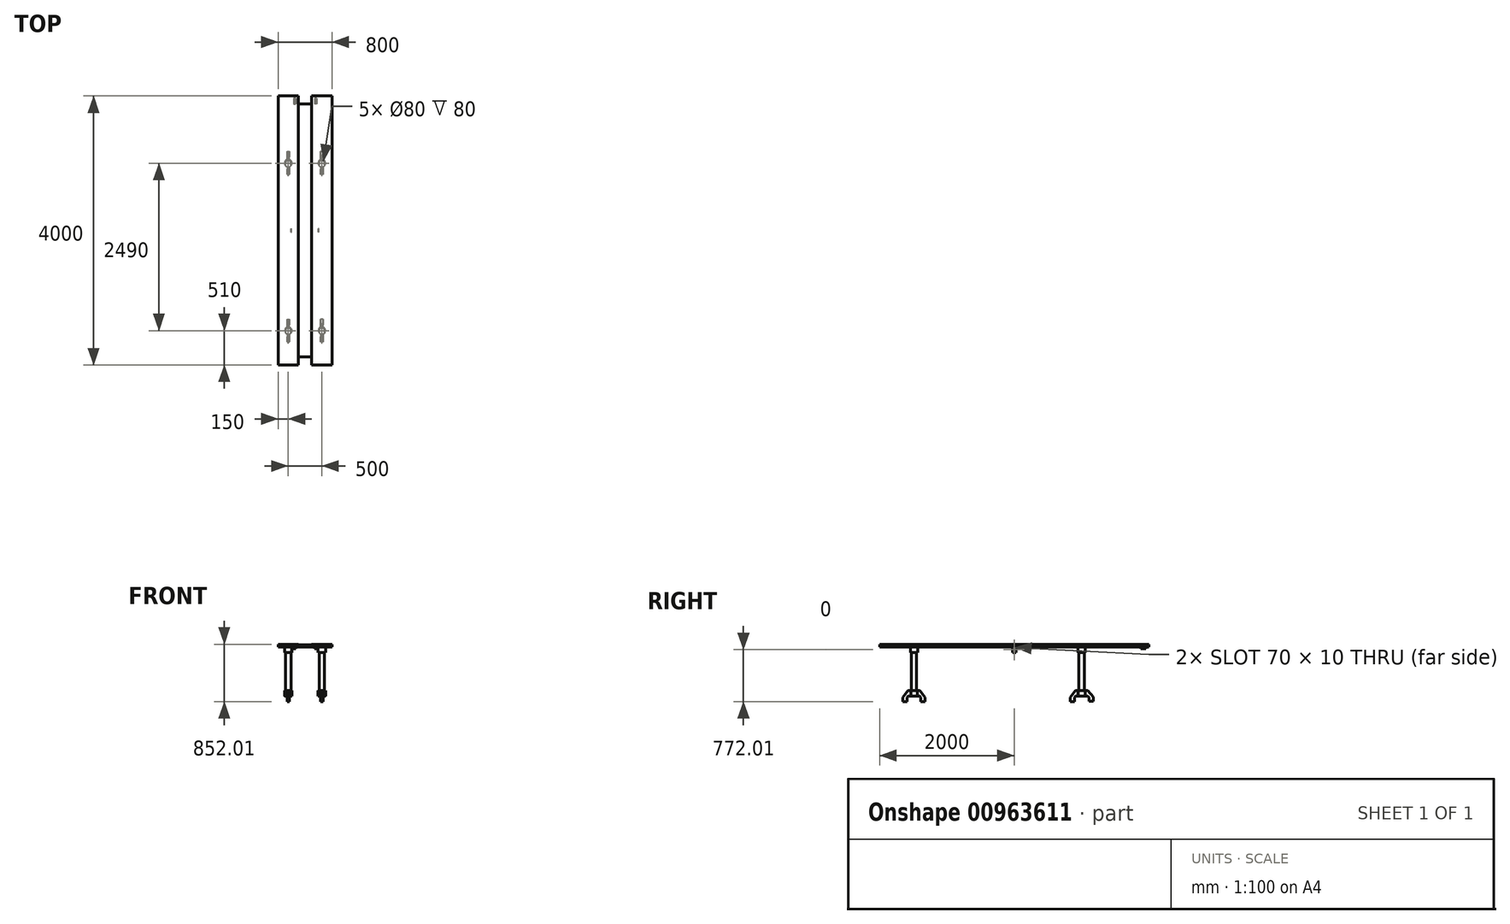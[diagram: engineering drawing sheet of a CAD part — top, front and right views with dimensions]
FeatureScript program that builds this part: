
annotation { "Feature Type Name" : "Feature", "Feature Type Description" : "" }
export const myFeature = defineFeature(function(context is Context, id is Id, definition is map)
    precondition{}
    {
        {
            var Q0;
            Q0=qCreatedBy(makeId("Front.planeOp"),FACE);
            var sketch = newSketch(context, id + "F0", { "sketchPlane" : qUnion([Q0])});
            skLineSegment(sketch, "E0", {"start": v(0, 63.58) * mm, "end": v(0, -44.48) * mm, "construction": true});
            skLineSegment(sketch, "E1", {"start": v(-61.04, 0) * mm, "end": v(60.75, 0) * mm, "construction": true});
            skLineSegment(sketch, "E2", {"start": v(-100, 20) * mm, "end": v(-400, 20) * mm});
            skLineSegment(sketch, "E3", {"start": v(-400, 20) * mm, "end": v(-400, -20) * mm});
            skLineSegment(sketch, "E4", {"start": v(-400, -20) * mm, "end": v(400, -20) * mm});
            skLineSegment(sketch, "E5", {"start": v(400, -20) * mm, "end": v(400, 20) * mm});
            skLineSegment(sketch, "E6", {"start": v(400, 20) * mm, "end": v(100, 20) * mm});
            skLineSegment(sketch, "E7", {"start": v(100, 20) * mm, "end": v(100, 10) * mm});
            skLineSegment(sketch, "E8", {"start": v(100, 10) * mm, "end": v(-100, 10) * mm});
            skLineSegment(sketch, "E9", {"start": v(-100, 10) * mm, "end": v(-100, 20) * mm});
            skSolve(sketch);
        }
        {
            var Q0;
            Q0 = qSketchRegion(id + "F0", true);
            extrude(context, id + "F1", {"entities" : qUnion([Q0]), "oppositeDirection" : true, "depth" : 4000 * mm, "offsetDistance" : 25.4 * mm});
        }
        {
            var Q0;
            Q0=makeQuery(id+"F1.opExtrude","SWEPT_FACE",FACE,{"disambiguationData":[OSD([sQuery(id+"F0.wireOp",EDGE,"E8")])]});
            var sketch = newSketch(context, id + "F2", { "sketchPlane" : qUnion([Q0])});
            skLineSegment(sketch, "E10.bottom", {"start": v(-100, 0) * mm, "end": v(100, 0) * mm});
            skLineSegment(sketch, "E10.top", {"start": v(-100, 120) * mm, "end": v(100, 120) * mm});
            skLineSegment(sketch, "E10.left", {"start": v(-100, 0) * mm, "end": v(-100, 120) * mm});
            skLineSegment(sketch, "E10.right", {"start": v(100, 0) * mm, "end": v(100, 120) * mm});
            skLineSegment(sketch, "E11.bottom", {"start": v(-100, 4000) * mm, "end": v(100, 4000) * mm});
            skLineSegment(sketch, "E11.top", {"start": v(-100, 3880) * mm, "end": v(100, 3880) * mm});
            skLineSegment(sketch, "E11.left", {"start": v(-100, 4000) * mm, "end": v(-100, 3880) * mm});
            skLineSegment(sketch, "E11.right", {"start": v(100, 4000) * mm, "end": v(100, 3880) * mm});
            skSolve(sketch);
        }
        {
            var Q0;
            Q0 = qSketchRegion(id + "F2", true);
            extrude(context, id + "F3", {"entities" : qUnion([Q0]), "operationType" : NewBodyOperationType.REMOVE, "oppositeDirection" : true, "depth" : 55.88 * mm, "offsetDistance" : 25.4 * mm});
        }
        {
            var Q0;
            Q0=makeQuery(id+"F3.boolean.opBoolean","COPY",EDGE,{"derivedFrom":makeQuery(id+"F3.opExtrude","CAP_EDGE",EDGE,{"disambiguationData":[OSD([sQuery(id+"F2.wireOp",EDGE,"E11.top")])],"isStart":true})});
            var Q1;
            Q1=makeQuery(id+"F3.boolean.opBoolean","COPY",EDGE,{"derivedFrom":makeQuery(id+"F3.opExtrude","CAP_EDGE",EDGE,{"disambiguationData":[OSD([sQuery(id+"F2.wireOp",EDGE,"E10.top")])],"isStart":true})});
            var Q2;
            Q2=makeQuery(id+"F3.boolean.opBoolean","INTERSECT",EDGE,{"derivedFrom":[makeQuery(id+"F1.opExtrude","SWEPT_FACE",FACE,{"disambiguationData":[OSD([sQuery(id+"F0.wireOp",EDGE,"E4")])]}),makeQuery(id+"F3.opExtrude","SWEPT_FACE",FACE,{"disambiguationData":[OSD([sQuery(id+"F2.wireOp",EDGE,"E10.top")])]})]});
            var Q3;
            Q3=makeQuery(id+"F3.boolean.opBoolean","INTERSECT",EDGE,{"derivedFrom":[makeQuery(id+"F1.opExtrude","SWEPT_FACE",FACE,{"disambiguationData":[OSD([sQuery(id+"F0.wireOp",EDGE,"E4")])]}),makeQuery(id+"F3.opExtrude","SWEPT_FACE",FACE,{"disambiguationData":[OSD([sQuery(id+"F2.wireOp",EDGE,"E11.top")])]})]});
            fillet(context, id + "F4", {"entities" : qUnion([Q0, Q1, Q2, Q3]), "radius" : 10 * mm, "tangentPropagation" : true, "allowEdgeOverflow" : false});
        }
        {
            var Q0;
            Q0=makeQuery(id+"F1.opExtrude","SWEPT_FACE",FACE,{"disambiguationData":[OSD([sQuery(id+"F0.wireOp",EDGE,"E4")])]});
            var sketch = newSketch(context, id + "F5", { "sketchPlane" : qUnion([Q0])});
            skCircle(sketch, "E12", {"center": v(-250, -510) * mm, "radius": 55 * mm});
            skPoint(sketch, "E12.centerSnap0", {"position": v(-250, 0) * mm});
            skCircle(sketch, "E13", {"center": v(-250, -3000) * mm, "radius": 55 * mm});
            skPoint(sketch, "E13.centerSnap0", {"position": v(-250, -4000) * mm});
            skLineSegment(sketch, "E14", {"start": v(0, 313.38) * mm, "end": v(0, -4618.74) * mm, "construction": true});
            skCircle(sketch, "E15.MirrorC", {"center": v(250, -510) * mm, "radius": 55 * mm});
            skCircle(sketch, "E16.MirrorC", {"center": v(250, -3000) * mm, "radius": 55 * mm});
            skCircle(sketch, "E17", {"center": v(-250, -3000) * mm, "radius": 40 * mm});
            skCircle(sketch, "E18", {"center": v(-250, -510) * mm, "radius": 40 * mm});
            skCircle(sketch, "E19", {"center": v(250, -510) * mm, "radius": 40 * mm});
            skCircle(sketch, "E20", {"center": v(250, -3000) * mm, "radius": 40 * mm});
            skSolve(sketch);
        }
        {
            var Q0;
            Q0 = qSketchRegion(id + "F5", true);
            extrude(context, id + "F6", {"entities" : qUnion([Q0]), "operationType" : NewBodyOperationType.ADD, "depth" : 80 * mm, "offsetDistance" : 25.4 * mm});
        }
        {
            var Q0;
            {var subQ0=sQuery(id+"F0.wireOp",EDGE,"E3");var subQ1=sQuery(id+"F0.wireOp",EDGE,"E4");Q0=makeQuery(id+"F6.boolean.opBoolean","SPLIT",FACE,{"disambiguationData":[TD([makeQuery(id+"F1.opExtrude","SWEPT_FACE",FACE,{"disambiguationData":[OSD([subQ0])]})])],"derivedFrom":makeQuery(id+"F1.opExtrude","SWEPT_FACE",FACE,{"disambiguationData":[OSD([subQ1])]})});}
            var sketch = newSketch(context, id + "F7", { "sketchPlane" : qUnion([Q0])});
            skLineSegment(sketch, "E21.bottom", {"start": v(-205, -1975) * mm, "end": v(-200, -1975) * mm});
            skLineSegment(sketch, "E21.top", {"start": v(-205, -2025) * mm, "end": v(-200, -2025) * mm});
            skLineSegment(sketch, "E21.left", {"start": v(-205, -1975) * mm, "end": v(-205, -2025) * mm});
            skLineSegment(sketch, "E21.right", {"start": v(-200, -1975) * mm, "end": v(-200, -2025) * mm});
            skLineSegment(sketch, "E22.bottom", {"start": v(205, -1975) * mm, "end": v(200, -1975) * mm});
            skLineSegment(sketch, "E22.top", {"start": v(205, -2025) * mm, "end": v(200, -2025) * mm});
            skLineSegment(sketch, "E22.left", {"start": v(205, -1975) * mm, "end": v(205, -2025) * mm});
            skLineSegment(sketch, "E22.right", {"start": v(200, -1975) * mm, "end": v(200, -2025) * mm});
            skLineSegment(sketch, "E23", {"start": v(-691.2, -2000) * mm, "end": v(786.12, -2000) * mm, "construction": true});
            skPoint(sketch, "E23.startSnap0", {"position": v(-400, -2000) * mm});
            skLineSegment(sketch, "E24", {"start": v(0, 1136.46) * mm, "end": v(0, -4393.14) * mm, "construction": true});
            skSolve(sketch);
        }
        {
            var Q0;
            Q0 = qSketchRegion(id + "F7", true);
            extrude(context, id + "F8", {"entities" : qUnion([Q0]), "operationType" : NewBodyOperationType.ADD, "depth" : 80 * mm, "offsetDistance" : 25.4 * mm});
        }
        {
            var Q0;
            Q0=makeQuery(id+"F8.opExtrude","SWEPT_FACE",FACE,{"disambiguationData":[OSD([sQuery(id+"F7.wireOp",EDGE,"E21.left")])]});
            var sketch = newSketch(context, id + "F9", { "sketchPlane" : qUnion([Q0])});
            skLineSegment(sketch, "E25", {"start": v(-2000, -30) * mm, "end": v(-2000, -90) * mm, "construction": true});
            skPoint(sketch, "E25.startSnap0", {"position": v(-2000, -100) * mm});
            skArc(sketch, "E26", {"start": v(-1995, -30) * mm, "mid": v(-2000, -25) * mm, "end": v(-2005, -30) * mm});
            skLineSegment(sketch, "E27", {"start": v(-2005, -30) * mm, "end": v(-2005, -90) * mm});
            skLineSegment(sketch, "E28", {"start": v(-1995, -30) * mm, "end": v(-1995, -90) * mm});
            skArc(sketch, "E29", {"start": v(-2005, -90) * mm, "mid": v(-2000, -95) * mm, "end": v(-1995, -90) * mm});
            skSolve(sketch);
        }
        {
            var Q0;
            Q0 = qSketchRegion(id + "F9", true);
            extrude(context, id + "F10", {"entities" : qUnion([Q0]), "operationType" : NewBodyOperationType.REMOVE, "endBound" : BoundingType.THROUGH_ALL, "oppositeDirection" : true, "depth" : 25.4 * mm, "offsetDistance" : 25.4 * mm});
        }
        {
            var Q0;
            Q0=makeQuery(id+"F6.boolean.opBoolean","SPLIT",FACE,{"disambiguationData":[TD([makeQuery(id+"F6.opExtrude","SWEPT_FACE",FACE,{"disambiguationData":[OSD([sQuery(id+"F5.wireOp",EDGE,"E20")])]})])],"derivedFrom":makeQuery(id+"F1.opExtrude","SWEPT_FACE",FACE,{"disambiguationData":[OSD([sQuery(id+"F0.wireOp",EDGE,"E4")])]})});
            var sketch = newSketch(context, id + "F11", { "sketchPlane" : qUnion([Q0])});
            skCircle(sketch, "E30", {"center": v(250, -3000) * mm, "radius": 40 * mm});
            skCircle(sketch, "E31", {"center": v(-250, -3000) * mm, "radius": 40 * mm});
            skCircle(sketch, "E32", {"center": v(-250, -510) * mm, "radius": 40 * mm});
            skCircle(sketch, "E33", {"center": v(250, -510) * mm, "radius": 40 * mm});
            skSolve(sketch);
        }
        {
            var Q0;
            Q0 = qSketchRegion(id + "F11", true);
            extrude(context, id + "F12", {"entities" : qUnion([Q0]), "operationType" : NewBodyOperationType.ADD, "depth" : 730 * mm, "offsetDistance" : 25.4 * mm});
        }
        {
            var Q0;
            Q0=makeQuery(id+"F12.opExtrude","CAP_FACE",FACE,{"disambiguationData":[OSD([sQuery(id+"F11.wireOp",EDGE,"E32")])],"isStart":false});
            var sketch = newSketch(context, id + "F13", { "sketchPlane" : qUnion([Q0])});
            skCircle(sketch, "E34", {"center": v(-250, -510) * mm, "radius": 40 * mm});
            skCircle(sketch, "E35", {"center": v(-250, -510) * mm, "radius": 50 * mm});
            skSolve(sketch);
        }
        {
            var Q0;
            Q0 = qSketchRegion(id + "F13", true);
            extrude(context, id + "F14", {"entities" : qUnion([Q0]), "oppositeDirection" : true, "depth" : 80 * mm, "offsetDistance" : 25.4 * mm});
        }
        {
            var Q0;
            Q0=makeQuery(id+"F14.opExtrude","CAP_EDGE",EDGE,{"disambiguationData":[OSD([sQuery(id+"F13.wireOp",EDGE,"E35")])],"isStart":true});
            cPlane(context, id + "F15", {"entities" : qUnion([Q0]), "cplaneType" : CPlaneType.LINE_ANGLE, "offset" : 25.4 * mm, "angle" : 0 * degree, "width" : 152.4 * mm, "height" : 152.4 * mm});
        }
        {
            var Q0;
            Q0=qCreatedBy(id+"F15.planeOp",FACE);
            var sketch = newSketch(context, id + "F16", { "sketchPlane" : qUnion([Q0])});
            skLineSegment(sketch, "E36", {"start": v(-558.17, -670) * mm, "end": v(-598.17, -670) * mm});
            skLineSegment(sketch, "E37", {"start": v(-598.17, -670) * mm, "end": v(-677, -767.01) * mm});
            skLineSegment(sketch, "E38", {"start": v(-677, -767.01) * mm, "end": v(-677, -832.01) * mm});
            skLineSegment(sketch, "E39", {"start": v(-677, -832.01) * mm, "end": v(-612, -832.01) * mm});
            skLineSegment(sketch, "E40", {"start": v(-612, -832.01) * mm, "end": v(-612, -767.01) * mm});
            skLineSegment(sketch, "E41", {"start": v(-612, -767.01) * mm, "end": v(-598.17, -750) * mm});
            skLineSegment(sketch, "E42", {"start": v(-598.17, -750) * mm, "end": v(-558.17, -750) * mm});
            skLineSegment(sketch, "E43", {"start": v(-558.17, -750) * mm, "end": v(-558.17, -670) * mm});
            skLineSegment(sketch, "E44", {"start": v(-462.75, -670) * mm, "end": v(-422.75, -670) * mm});
            skLineSegment(sketch, "E45", {"start": v(-422.75, -670) * mm, "end": v(-343.93, -767.01) * mm});
            skLineSegment(sketch, "E46", {"start": v(-343.93, -767.01) * mm, "end": v(-343.93, -832.01) * mm});
            skLineSegment(sketch, "E47", {"start": v(-343.93, -832.01) * mm, "end": v(-408.93, -832.01) * mm});
            skLineSegment(sketch, "E48", {"start": v(-408.93, -832.01) * mm, "end": v(-408.93, -767.01) * mm});
            skLineSegment(sketch, "E49", {"start": v(-408.93, -767.01) * mm, "end": v(-422.75, -750) * mm});
            skLineSegment(sketch, "E50", {"start": v(-422.75, -750) * mm, "end": v(-462.75, -750) * mm});
            skLineSegment(sketch, "E51", {"start": v(-462.75, -750) * mm, "end": v(-462.75, -670) * mm});
            skSolve(sketch);
        }
        {
            var Q0;
            Q0 = qSketchRegion(id + "F16", true);
            extrude(context, id + "F17", {"entities" : qUnion([Q0]), "operationType" : NewBodyOperationType.ADD, "endBound" : BoundingType.SYMMETRIC, "depth" : 33 * mm, "offsetDistance" : 25.4 * mm});
        }
        {
            var Q0;
            Q0=makeQuery(id+"F14.opExtrude","SWEPT_BODY",BODY,{"disambiguationData":[OSD([sQuery(id+"F13.wireOp",EDGE,"E34"),sQuery(id+"F13.wireOp",EDGE,"E35")])]});
            var Q1;
            Q1=qCreatedBy(makeId("Right.planeOp"),FACE);
            mirror(context, id + "F18", {"entities" : qUnion([Q0]), "mirrorPlane" : qUnion([Q1])});
        }
        {
            var Q0;
            Q0=makeQuery(id+"F12.opExtrude","CAP_FACE",FACE,{"disambiguationData":[OSD([sQuery(id+"F11.wireOp",EDGE,"E30")])],"isStart":false});
            var sketch = newSketch(context, id + "F19", { "sketchPlane" : qUnion([Q0])});
            skCircle(sketch, "E52", {"center": v(-250, -3000) * mm, "radius": 40 * mm});
            skCircle(sketch, "E53", {"center": v(-250, -3000) * mm, "radius": 55 * mm});
            skSolve(sketch);
        }
        {
            var Q0;
            Q0 = qSketchRegion(id + "F19", true);
            extrude(context, id + "F20", {"entities" : qUnion([Q0]), "oppositeDirection" : true, "depth" : 80 * mm, "offsetDistance" : 25.4 * mm});
        }
        {
            var Q0;
            Q0=makeQuery(id+"F20.opExtrude","SWEPT_BODY",BODY,{"disambiguationData":[OSD([sQuery(id+"F19.wireOp",EDGE,"E52"),sQuery(id+"F19.wireOp",EDGE,"E53")])]});
            var Q1;
            Q1=qCreatedBy(makeId("Right.planeOp"),FACE);
            mirror(context, id + "F21", {"entities" : qUnion([Q0]), "mirrorPlane" : qUnion([Q1])});
        }
        {
            var Q0;
            Q0=makeQuery(id+"F20.opExtrude","CAP_EDGE",EDGE,{"disambiguationData":[OSD([sQuery(id+"F19.wireOp",EDGE,"E53")])],"isStart":true});
            cPlane(context, id + "F22", {"entities" : qUnion([Q0]), "cplaneType" : CPlaneType.LINE_ANGLE, "offset" : 25.4 * mm, "angle" : 0 * degree, "width" : 152.4 * mm, "height" : 152.4 * mm});
        }
        {
            var Q0;
            Q0=qCreatedBy(id+"F22.planeOp",FACE);
            var sketch = newSketch(context, id + "F23", { "sketchPlane" : qUnion([Q0])});
            skLineSegment(sketch, "E54", {"start": v(-2949.5, -670) * mm, "end": v(-2909.5, -670) * mm});
            skLineSegment(sketch, "E55", {"start": v(-2909.5, -670) * mm, "end": v(-2830.68, -767.01) * mm});
            skLineSegment(sketch, "E56", {"start": v(-2830.68, -767.01) * mm, "end": v(-2830.68, -832.01) * mm});
            skLineSegment(sketch, "E57", {"start": v(-2830.68, -832.01) * mm, "end": v(-2895.68, -832.01) * mm});
            skLineSegment(sketch, "E58", {"start": v(-2895.68, -832.01) * mm, "end": v(-2895.68, -767.01) * mm});
            skLineSegment(sketch, "E59", {"start": v(-2895.68, -767.01) * mm, "end": v(-2909.5, -750) * mm});
            skLineSegment(sketch, "E60", {"start": v(-2909.5, -750) * mm, "end": v(-2949.5, -750) * mm});
            skLineSegment(sketch, "E61", {"start": v(-2949.5, -750) * mm, "end": v(-2949.5, -670) * mm});
            skLineSegment(sketch, "E62", {"start": v(-3050.57, -670) * mm, "end": v(-3090.57, -670) * mm});
            skLineSegment(sketch, "E63", {"start": v(-3090.57, -670) * mm, "end": v(-3176.12, -761.14) * mm});
            skLineSegment(sketch, "E64", {"start": v(-3176.12, -761.14) * mm, "end": v(-3176.12, -826.14) * mm});
            skLineSegment(sketch, "E65", {"start": v(-3176.12, -826.14) * mm, "end": v(-3111.12, -826.14) * mm});
            skLineSegment(sketch, "E66", {"start": v(-3111.12, -826.14) * mm, "end": v(-3111.12, -771.89) * mm});
            skLineSegment(sketch, "E67", {"start": v(-3111.12, -771.89) * mm, "end": v(-3090.57, -750) * mm});
            skLineSegment(sketch, "E68", {"start": v(-3090.57, -750) * mm, "end": v(-3050.57, -750) * mm});
            skLineSegment(sketch, "E69", {"start": v(-3050.57, -750) * mm, "end": v(-3050.57, -670) * mm});
            skSolve(sketch);
        }
        {
            var Q0;
            Q0 = qSketchRegion(id + "F23", true);
            extrude(context, id + "F24", {"entities" : qUnion([Q0]), "operationType" : NewBodyOperationType.ADD, "endBound" : BoundingType.SYMMETRIC, "depth" : 33 * mm, "offsetDistance" : 25.4 * mm});
        }
        {
            var Q0;
            Q0=makeQuery(id+"F20.opExtrude","SWEPT_BODY",BODY,{"disambiguationData":[OSD([sQuery(id+"F19.wireOp",EDGE,"E52"),sQuery(id+"F19.wireOp",EDGE,"E53")])]});
            var Q1;
            Q1=qCreatedBy(makeId("Right.planeOp"),FACE);
            mirror(context, id + "F25", {"entities" : qUnion([Q0]), "mirrorPlane" : qUnion([Q1])});
        }
        {
            var Q0;
            {var subQ0=sQuery(id+"F0.wireOp",EDGE,"E3");var subQ1=sQuery(id+"F0.wireOp",EDGE,"E4");Q0=makeQuery(id+"F6.boolean.opBoolean","SPLIT",FACE,{"disambiguationData":[TD([makeQuery(id+"F1.opExtrude","SWEPT_FACE",FACE,{"disambiguationData":[OSD([subQ0])]})])],"derivedFrom":makeQuery(id+"F1.opExtrude","SWEPT_FACE",FACE,{"disambiguationData":[OSD([subQ1])]})});}
            var sketch = newSketch(context, id + "F26", { "sketchPlane" : qUnion([Q0])});
            skLineSegment(sketch, "E70.bottom", {"start": v(145, -3960) * mm, "end": v(140, -3960) * mm});
            skLineSegment(sketch, "E70.top", {"start": v(145, -3880) * mm, "end": v(140, -3880) * mm});
            skLineSegment(sketch, "E70.left", {"start": v(145, -3960) * mm, "end": v(145, -3880) * mm});
            skLineSegment(sketch, "E70.right", {"start": v(140, -3960) * mm, "end": v(140, -3880) * mm});
            skLineSegment(sketch, "E71.bottom", {"start": v(-140, -3960) * mm, "end": v(-145, -3960) * mm});
            skLineSegment(sketch, "E71.top", {"start": v(-140, -3880) * mm, "end": v(-145, -3880) * mm});
            skLineSegment(sketch, "E71.left", {"start": v(-140, -3960) * mm, "end": v(-140, -3880) * mm});
            skLineSegment(sketch, "E71.right", {"start": v(-145, -3960) * mm, "end": v(-145, -3880) * mm});
            skSolve(sketch);
        }
        {
            var Q0;
            Q0 = qSketchRegion(id + "F26", true);
            extrude(context, id + "F27", {"entities" : qUnion([Q0]), "operationType" : NewBodyOperationType.ADD, "depth" : 25.4 * mm, "offsetDistance" : 25.4 * mm});
        }
        {
            var Q0;
            Q0=makeQuery(id+"F27.opExtrude","SWEPT_FACE",FACE,{"disambiguationData":[OSD([sQuery(id+"F26.wireOp",EDGE,"E71.right")])]});
            var sketch = newSketch(context, id + "F28", { "sketchPlane" : qUnion([Q0])});
            skLineSegment(sketch, "E72.bottom", {"start": v(-3960, -45.4) * mm, "end": v(-3880, -45.4) * mm});
            skLineSegment(sketch, "E72.top", {"start": v(-3960, -40.4) * mm, "end": v(-3880, -40.4) * mm});
            skLineSegment(sketch, "E72.left", {"start": v(-3960, -45.4) * mm, "end": v(-3960, -40.4) * mm});
            skLineSegment(sketch, "E72.right", {"start": v(-3880, -45.4) * mm, "end": v(-3880, -40.4) * mm});
            skSolve(sketch);
        }
        {
            var Q0;
            Q0 = qSketchRegion(id + "F28", true);
            extrude(context, id + "F29", {"entities" : qUnion([Q0]), "operationType" : NewBodyOperationType.ADD, "depth" : 25.4 * mm, "offsetDistance" : 25.4 * mm});
        }
        {
            var Q0;
            Q0=makeQuery(id+"F27.opExtrude","SWEPT_FACE",FACE,{"disambiguationData":[OSD([sQuery(id+"F26.wireOp",EDGE,"E70.left")])]});
            var sketch = newSketch(context, id + "F30", { "sketchPlane" : qUnion([Q0])});
            skLineSegment(sketch, "E73.bottom", {"start": v(3960, -45.4) * mm, "end": v(3880, -45.4) * mm});
            skLineSegment(sketch, "E73.top", {"start": v(3960, -40.4) * mm, "end": v(3880, -40.4) * mm});
            skLineSegment(sketch, "E73.left", {"start": v(3960, -45.4) * mm, "end": v(3960, -40.4) * mm});
            skLineSegment(sketch, "E73.right", {"start": v(3880, -45.4) * mm, "end": v(3880, -40.4) * mm});
            skSolve(sketch);
        }
        {
            var Q0;
            Q0 = qSketchRegion(id + "F30", true);
            extrude(context, id + "F31", {"entities" : qUnion([Q0]), "operationType" : NewBodyOperationType.ADD, "depth" : 25.4 * mm, "offsetDistance" : 25.4 * mm});
        }
    });
